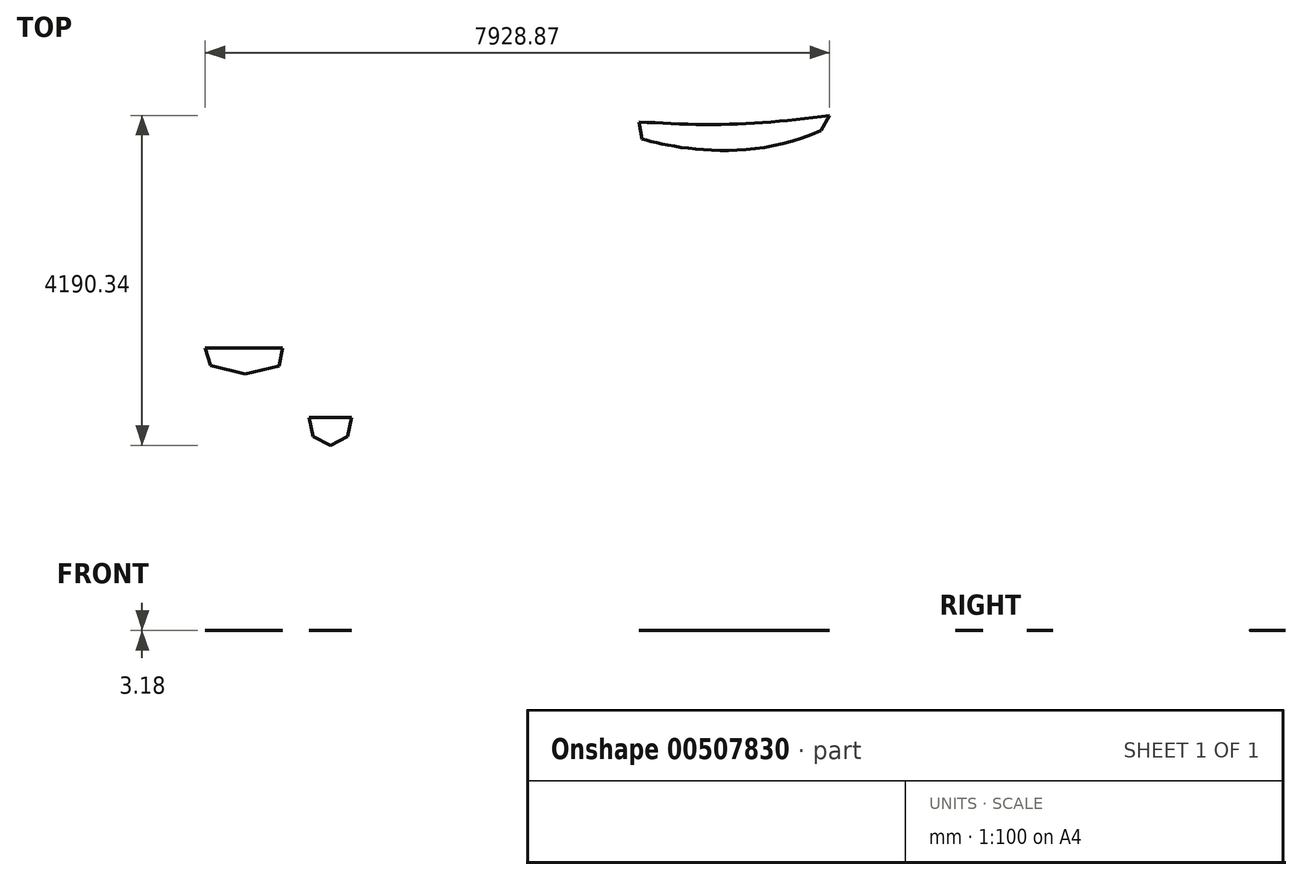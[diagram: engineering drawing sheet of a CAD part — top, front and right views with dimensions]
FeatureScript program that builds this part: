
annotation { "Feature Type Name" : "Feature", "Feature Type Description" : "" }
export const myFeature = defineFeature(function(context is Context, id is Id, definition is map)
    precondition{}
    {
        {
            var Q0;
            Q0=qCreatedBy(makeId("Top.planeOp"),FACE);
            var sketch = newSketch(context, id + "F0", { "sketchPlane" : qUnion([Q0])});
            skLineSegment(sketch, "E0", {"start": v(-502.7, 182.94) * mm, "end": v(478.38, 182.94) * mm});
            skLineSegment(sketch, "E1", {"start": v(-502.7, 182.94) * mm, "end": v(-436.56, -39.31) * mm});
            skLineSegment(sketch, "E2", {"start": v(436.56, -45.15) * mm, "end": v(478.38, 182.94) * mm});
            skLineSegment(sketch, "E3", {"start": v(-436.56, -39.31) * mm, "end": v(0, -147.26) * mm});
            skLineSegment(sketch, "E4", {"start": v(0, -147.26) * mm, "end": v(436.56, -45.15) * mm});
            skLineSegment(sketch, "E5", {"start": v(-215.75, -623.44) * mm, "end": v(324, -623.44) * mm});
            skLineSegment(sketch, "E6", {"start": v(324, -623.44) * mm, "end": v(324, -861.57) * mm});
            skLineSegment(sketch, "E7", {"start": v(324, -861.57) * mm, "end": v(0, -961.57) * mm});
            skLineSegment(sketch, "E8", {"start": v(0, -961.57) * mm, "end": v(-325.85, -834.58) * mm});
            skLineSegment(sketch, "E9", {"start": v(-325.85, -834.58) * mm, "end": v(-215.75, -623.44) * mm});
            skLineSegment(sketch, "E10", {"start": v(-325.85, -834.58) * mm, "end": v(324, -861.57) * mm, "construction": true});
            skLineSegment(sketch, "E11", {"start": v(0, -147.26) * mm, "end": v(474.48, -147.26) * mm, "construction": true});
            skLineSegment(sketch, "E12", {"start": v(436.56, -153.1) * mm, "end": v(436.56, -45.15) * mm, "construction": true});
            skLineSegment(sketch, "E13", {"start": v(-325.85, -834.58) * mm, "end": v(-330.46, -945.61) * mm, "construction": true});
            skLineSegment(sketch, "E14", {"start": v(-330.46, -945.61) * mm, "end": v(0, -961.57) * mm, "construction": true});
            skLineSegment(sketch, "E15", {"start": v(0, -961.57) * mm, "end": v(5.47, -848.34) * mm, "construction": true});
            skLineSegment(sketch, "E16.bottom", {"start": v(1671.84, 3348.7) * mm, "end": v(7392.84, 3328.65) * mm, "construction": true});
            skLineSegment(sketch, "E16.right", {"start": v(7392.84, 3328.65) * mm, "end": v(7397.92, 3299.58) * mm, "construction": true});
            skLineSegment(sketch, "E17", {"start": v(7113.44, 3329.63) * mm, "end": v(7113.44, 3097.85) * mm, "construction": true});
            skLineSegment(sketch, "E18", {"start": v(6808.64, 3330.7) * mm, "end": v(6808.64, 3065.58) * mm, "construction": true});
            skLineSegment(sketch, "E19", {"start": v(6503.85, 3331.76) * mm, "end": v(6502.83, 3042.84) * mm, "construction": true});
            skLineSegment(sketch, "E20", {"start": v(6199.05, 3332.83) * mm, "end": v(6197.98, 3028.03) * mm, "construction": true});
            skLineSegment(sketch, "E21", {"start": v(5894.25, 3333.9) * mm, "end": v(5894.25, 3019.57) * mm, "construction": true});
            skLineSegment(sketch, "E22", {"start": v(5589.45, 3334.97) * mm, "end": v(5589.45, 3027) * mm, "construction": true});
            skLineSegment(sketch, "E23", {"start": v(5284.65, 3336.04) * mm, "end": v(5283.62, 3040.76) * mm, "construction": true});
            skLineSegment(sketch, "E24", {"start": v(5005.25, 3337.01) * mm, "end": v(5004.26, 3054.44) * mm, "construction": true});
            skLineSegment(sketch, "E25", {"start": v(830.58, -697.62) * mm, "end": v(1341.75, -697.62) * mm, "construction": true});
            skLineSegment(sketch, "E26", {"start": v(1341.75, -697.62) * mm, "end": v(1292.54, -929.4) * mm, "construction": true});
            skLineSegment(sketch, "E27", {"start": v(1292.54, -929.4) * mm, "end": v(1086.16, -1035.77) * mm, "construction": true});
            skLineSegment(sketch, "E28", {"start": v(1086.16, -1035.77) * mm, "end": v(879.79, -929.4) * mm, "construction": true});
            skLineSegment(sketch, "E29", {"start": v(879.79, -929.4) * mm, "end": v(830.58, -697.62) * mm, "construction": true});
            skLineSegment(sketch, "E30", {"start": v(830.58, -697.62) * mm, "end": v(830.58, -1104.47) * mm, "construction": true});
            skLineSegment(sketch, "E31", {"start": v(830.58, -1104.47) * mm, "end": v(1341.75, -1104.47) * mm, "construction": true});
            skLineSegment(sketch, "E32", {"start": v(1341.75, -1104.47) * mm, "end": v(1341.75, -697.62) * mm, "construction": true});
            skLineSegment(sketch, "E33", {"start": v(879.79, -929.4) * mm, "end": v(1292.54, -929.4) * mm, "construction": true});
            skLineSegment(sketch, "E34", {"start": v(1086.16, -1035.77) * mm, "end": v(1086.16, -929.4) * mm, "construction": true});
            skLineSegment(sketch, "E35", {"start": v(941.9, -929.4) * mm, "end": v(941.9, -697.62) * mm, "construction": true});
            skLineSegment(sketch, "E36", {"start": v(1086.16, -1104.47) * mm, "end": v(1086.16, -1035.77) * mm, "construction": true});
            skLineSegment(sketch, "E37", {"start": v(814.6, -700.89) * mm, "end": v(866.25, -939.01) * mm});
            skLineSegment(sketch, "E38", {"start": v(866.25, -939.01) * mm, "end": v(1086.16, -1052.19) * mm});
            skLineSegment(sketch, "E39", {"start": v(1086.16, -1052.19) * mm, "end": v(1303.4, -939.01) * mm});
            skLineSegment(sketch, "E40", {"start": v(1303.4, -939.01) * mm, "end": v(1355.05, -700.89) * mm});
            skLineSegment(sketch, "E41", {"start": v(1355.05, -700.89) * mm, "end": v(814.6, -700.89) * mm});
            skLineSegment(sketch, "E42", {"start": v(1355.05, -700.89) * mm, "end": v(1355.05, -939.01) * mm, "construction": true});
            skLineSegment(sketch, "E43", {"start": v(1355.05, -939.01) * mm, "end": v(1303.4, -939.01) * mm, "construction": true});
            skLineSegment(sketch, "E44", {"start": v(814.6, -700.89) * mm, "end": v(814.6, -939.01) * mm, "construction": true});
            skLineSegment(sketch, "E45", {"start": v(814.6, -939.01) * mm, "end": v(866.25, -939.01) * mm, "construction": true});
            skFitSpline(sketch, "E46", {"points": [v(5004.26, 3054.44) * mm, v(5283.62, 3040.76) * mm, v(5589.45, 3027) * mm, v(5894.25, 3019.57) * mm, v(6197.98, 3028.03) * mm, v(6502.83, 3042.84) * mm, v(6808.64, 3065.58) * mm, v(7113.44, 3097.85) * mm, v(7426.17, 3138.15) * mm], "startDerivative": vector(2428.45, -99.8) * mm, "endDerivative": vector(2280.3, 419.02) * mm});
            skLineSegment(sketch, "E47", {"start": v(5283.62, 3040.76) * mm, "end": v(5282.72, 2783.59) * mm, "construction": true});
            skLineSegment(sketch, "E48", {"start": v(5589.45, 3027) * mm, "end": v(5589.45, 2731.72) * mm, "construction": true});
            skLineSegment(sketch, "E49", {"start": v(5894.25, 3019.57) * mm, "end": v(5894.25, 2705.25) * mm, "construction": true});
            skLineSegment(sketch, "E50", {"start": v(6197.98, 3028.03) * mm, "end": v(6196.86, 2707.36) * mm, "construction": true});
            skLineSegment(sketch, "E51", {"start": v(6502.83, 3042.84) * mm, "end": v(6501.75, 2734.87) * mm, "construction": true});
            skLineSegment(sketch, "E52", {"start": v(6808.64, 3065.58) * mm, "end": v(6808.64, 2776.66) * mm, "construction": true});
            skLineSegment(sketch, "E53", {"start": v(7113.44, 3097.85) * mm, "end": v(7113.44, 2872.43) * mm, "construction": true});
            skLineSegment(sketch, "E54", {"start": v(7426.17, 3138.15) * mm, "end": v(7319.28, 2946.91) * mm});
            skLineSegment(sketch, "E55", {"start": v(873.16, 996.57) * mm, "end": v(3590.96, 996.57) * mm, "construction": true});
            skFitSpline(sketch, "E56", {"points": [v(873.16, 996.57) * mm, v(3590.96, 996.57) * mm], "startDerivative": vector(2120.06, -869.1) * mm, "endDerivative": vector(722.87, 500.53) * mm});
            skArc(sketch, "E57", {"start": v(478.38, 182.94) * mm, "mid": v(-12.16, 199.9) * mm, "end": v(-502.7, 182.94) * mm, "construction": true});
            skLineSegment(sketch, "E58", {"start": v(0, -147.26) * mm, "end": v(-436.56, -147.26) * mm, "construction": true});
            skLineSegment(sketch, "E59", {"start": v(-436.56, -147.26) * mm, "end": v(-436.56, -39.31) * mm, "construction": true});
            skLineSegment(sketch, "E60", {"start": v(-502.7, 182.94) * mm, "end": v(-502.7, -147.26) * mm, "construction": true});
            skLineSegment(sketch, "E61", {"start": v(-502.7, -147.26) * mm, "end": v(-436.56, -147.26) * mm, "construction": true});
            skLineSegment(sketch, "E62", {"start": v(0, -147.26) * mm, "end": v(0, 182.94) * mm, "construction": true});
            skLineSegment(sketch, "E63", {"start": v(-2863.5, 1398.41) * mm, "end": v(-1882.42, 1398.41) * mm});
            skLineSegment(sketch, "E64", {"start": v(-2863.5, 1398.41) * mm, "end": v(-2770.33, 1180.13) * mm});
            skLineSegment(sketch, "E65", {"start": v(-2372.96, 1398.41) * mm, "end": v(-2372.96, 839.41) * mm, "construction": true});
            skLineSegment(sketch, "E66", {"start": v(-2770.33, 1180.13) * mm, "end": v(-2372.96, 1072.18) * mm});
            skLineSegment(sketch, "E67", {"start": v(-2372.96, 1072.18) * mm, "end": v(-2770.33, 1072.18) * mm, "construction": true});
            skLineSegment(sketch, "E68", {"start": v(-2770.33, 1072.18) * mm, "end": v(-2770.33, 1180.13) * mm, "construction": true});
            skLineSegment(sketch, "E69", {"start": v(-2770.33, 1180.13) * mm, "end": v(-2770.33, 1398.41) * mm, "construction": true});
            skLineSegment(sketch, "E70", {"start": v(-2770.33, 1180.13) * mm, "end": v(-2883.49, 1180.13) * mm, "construction": true});
            skLineSegment(sketch, "E71", {"start": v(-2883.49, 1180.13) * mm, "end": v(-2883.49, 1398.41) * mm, "construction": true});
            skLineSegment(sketch, "E72", {"start": v(-2883.49, 1398.41) * mm, "end": v(-2863.5, 1398.41) * mm, "construction": true});
            skLineSegment(sketch, "E73.MirrorCS", {"start": v(-1882.42, 1398.41) * mm, "end": v(-1975.59, 1180.13) * mm});
            skLineSegment(sketch, "E74.MirrorCS", {"start": v(-1975.59, 1180.13) * mm, "end": v(-2372.96, 1072.18) * mm});
            skLineSegment(sketch, "E75", {"start": v(5004.26, 3054.44) * mm, "end": v(5046.35, 2836.21) * mm});
            skLineSegment(sketch, "E76", {"start": v(4005.6, 6381.78) * mm, "end": v(6393.02, 6411.83) * mm, "construction": true});
            skFitSpline(sketch, "E77", {"points": [v(5046.35, 2836.21) * mm, v(7319.28, 2946.91) * mm], "startDerivative": vector(1165.51, -313.48) * mm, "endDerivative": vector(2788.72, 1269.46) * mm});
            skSolve(sketch);
        }
        {
            var Q0;
            Q0=makeQuery(id+"F0.imprint","IMPRINT",FACE,{"disambiguationData":[TD([[makeQuery(id+"F0.imprint","IMPRINT",EDGE,{"derivedFrom":sQuery(id+"F0.wireOp",EDGE,"E0")}),-1.0]])]});
            var Q1;
            Q1=makeQuery(id+"F0.imprint","IMPRINT",FACE,{"disambiguationData":[TD([[makeQuery(id+"F0.imprint","IMPRINT",EDGE,{"derivedFrom":sQuery(id+"F0.wireOp",EDGE,"E37")}),1.0]])]});
            var Q2;
            Q2=makeQuery(id+"F0.imprint","IMPRINT",FACE,{"disambiguationData":[TD([[makeQuery(id+"F0.imprint","IMPRINT",EDGE,{"derivedFrom":sQuery(id+"F0.wireOp",EDGE,"E46")}),-1.0]])]});
            extrude(context, id + "F1", {"entities" : qUnion([Q0, Q1, Q2]), "depth" : 3.17 * mm, "offsetDistance" : 25.4 * mm});
        }
    });
